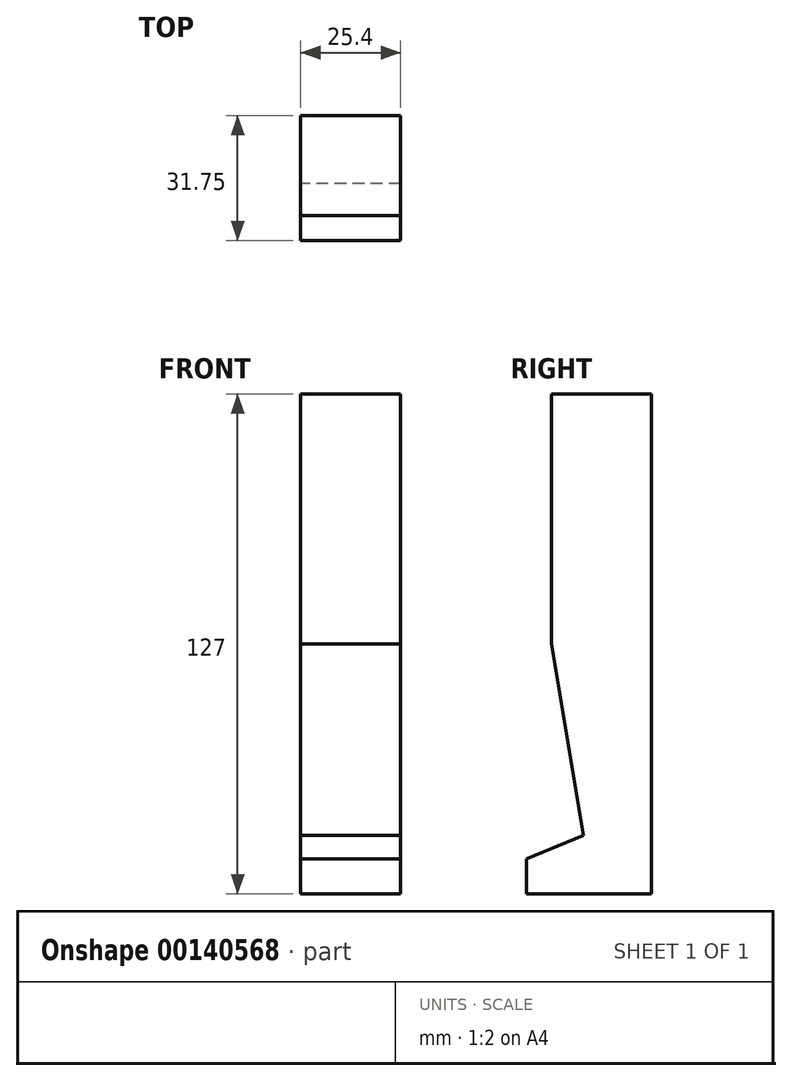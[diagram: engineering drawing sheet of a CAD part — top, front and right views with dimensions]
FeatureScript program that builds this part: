
annotation { "Feature Type Name" : "Feature", "Feature Type Description" : "" }
export const myFeature = defineFeature(function(context is Context, id is Id, definition is map)
    precondition{}
    {
        {
            var Q0;
            Q0=qCreatedBy(makeId("Right.planeOp"),FACE);
            var sketch = newSketch(context, id + "F0", { "sketchPlane" : qUnion([Q0])});
            skLineSegment(sketch, "E0", {"start": v(-12.7, 0) * mm, "end": v(-12.7, 63.5) * mm});
            skLineSegment(sketch, "E1", {"start": v(-12.7, 63.5) * mm, "end": v(12.7, 63.5) * mm});
            skLineSegment(sketch, "E2", {"start": v(12.7, 63.5) * mm, "end": v(12.7, 0) * mm});
            skLineSegment(sketch, "E3", {"start": v(12.7, 0) * mm, "end": v(12.7, -63.5) * mm});
            skLineSegment(sketch, "E4", {"start": v(12.7, -63.5) * mm, "end": v(-19.05, -63.5) * mm});
            skLineSegment(sketch, "E5", {"start": v(-19.05, -63.5) * mm, "end": v(-19.05, -54.6) * mm});
            skLineSegment(sketch, "E6", {"start": v(-19.05, -54.6) * mm, "end": v(-4.57, -48.67) * mm});
            skLineSegment(sketch, "E7", {"start": v(-4.57, -48.67) * mm, "end": v(-12.7, 0) * mm});
            skLineSegment(sketch, "E8", {"start": v(-12.7, 0) * mm, "end": v(12.7, 0) * mm, "construction": true});
            skSolve(sketch);
        }
        {
            var Q0;
            Q0=qSketchRegion(id+"F0",true);
            extrude(context, id + "F1", {"entities" : qUnion([Q0]), "depth" : 25.4 * mm});
        }
    });
